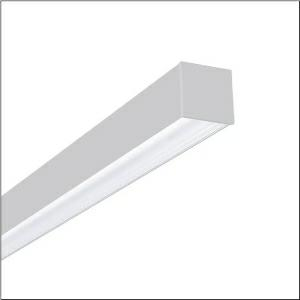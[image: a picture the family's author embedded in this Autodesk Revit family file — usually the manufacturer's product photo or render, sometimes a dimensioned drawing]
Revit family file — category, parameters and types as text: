
# Revit family: silica_r_5mx21bd1w4a_a515
name_source: partatom
category: Lighting Fixtures
units: mm (PartAtom-declared; Revit-internal decimal feet)

## family parameters
Cut with Voids When Loaded = No
Host = Face
Light Source = No
Part Type = Normal
Room Calculation Point = No
Round Connector Dimension = Use Diameter
Shared = No

## types (1)
- --- (1 x LED, 4950 lm, 29.3 W, 4000K)
    Apparent Load = 29 VA
    CIE Flux Codes = 82 97 100 100 100
    Color Rendering = 80
    Color Temperature = 4000K
    Default Elevation = 1800 mm
    Description = Silica®, office luminaire, of aluminium, light emission: direct distribution, primary light characteristic: symmetric, installation type: surface-mounted, LED rated luminous flux: 4.950 lm, light colour: 840, colour temperature: 4000K, control gear: ECG DALI, with terminal, 3+2-pole, max. 2.5mm², mains connection: 230V, AC, 50/60Hz, rated input power: 29W, luminaire housing, of aluminium, traffic white (RAL 9016), length: 1.440 mm, width: 64 mm, height: 64mm, protection rating (complete): IP20, insulation class (complete): insulation class I (protective earthing), certification: CE, permissible ambient temperature for indoor applications: 0..+35°C, standard: EN 50419, packaging unit: 1 piece
    Height = 64 mm
    Lamp = 1 x LED
    Lamp Light Flux = 4950 lm
    Lamp Power = 29.3 W
    Lamp count = 1
    Length = 1442 mm
    Luminous efficacy = 169 lm/W
    Manufacturer = Siteco
    ModVariant = No
    Model = 5MX21BD1W4A
    Mounting Place = Ceiling
    Mounting Type = Surface mounted
    Number of Poles = 1
    OnlyDefault = Yes
    Power Factor = 1
    Product Name = Silica®
    Product group = office luminaire | ceiling mounted
    ProductGroupID = 302
    Protection Class = Protection class I
    Protection Degree = IP 20
    RLX_Detail_Level = 1
    RlxData = <blob elided: 23389 chars, md5=e8684c15>
    Socket = socket
    Standby Power = 0 W
    System Light Flux = 4950 lm
    System Power = 29 W
    Type Comments = factory setting: luminous flux: 100 % | dim-lin: 254 | 163 mA
    Type Image = l_1003937.jpg
    URL = http://relux.com
    VarID = @adj_132106
    Voltage = 0 V
    Weight = 0.00 kg
    Width = 66 mm

## geometry (parser evidence)
native form markers: Blend x4, Sweep x11
no freeform markers — native parametric forms only
